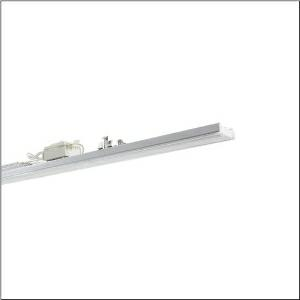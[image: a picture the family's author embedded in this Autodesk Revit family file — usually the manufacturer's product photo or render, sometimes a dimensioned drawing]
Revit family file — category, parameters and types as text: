
# Revit family: licross_r__11_recessed_ho_51tl12dv4m2md_61bc
name_source: partatom
category: Lighting Fixtures
units: mm (PartAtom-declared; Revit-internal decimal feet)

## family parameters
Cut with Voids When Loaded = No
Host = Face
Light Source = No
Part Type = Normal
Room Calculation Point = No
Round Connector Dimension = Use Diameter
Shared = No

## types (1)
- --- (1 x LED, 4070 lm, 21.7 W, 4000K)
    Apparent Load = 22 VA
    CIE Flux Codes = 66 91 98 100 100
    Color Rendering = 80
    Color Temperature = 4000K
    Default Elevation = 1800 mm
    Description = Licross® 11 Recessed HO, luminaire insert, of sheet steel, coil coated, white, length: 2.250mm, width: 66mm, height: 67mm, LED rated luminous flux: 27.150lm, light colour: 840, control gear: DALI 2 (for two DALI lines), with plug, 6-pole, with phase selection, mains connection: 220..240V, AC/DC, 0/50..60Hz, rated input power: 151W, without changeover relay, for emergency light function, for central battery installations according to DIN EN 60598-2-22, halogen-free wiring, primary optical cover: cover, of PMMA, light emission: direct distribution, primary light characteristic: symmetric, protection rating (complete): IP40, insulation class (complete): insulation class I (protective earthing), certification: CE, ENEC, VDE, UKCA, protection symbol: D if used in an environment without relevant dust loads with corresponding accessories, impact resistance: IK06, permissible ambient temperature for indoor applications: -40..+35°C, standard: EN 60598-2-22, corresponds to IFS (International Featured Standards) requirements for safety and quality in the food industry, reducing of maximum allowable ambient temperature of 5°C with ceiling mounting, LABS conformity tested according to VDMA 24364:2018-05, packaging unit: 1 piece
    Height = 58 mm
    Lamp = 1 x LED
    Lamp Light Flux = 4070 lm
    Lamp Power = 21.7 W
    Lamp count = 1
    Length = 2250 mm
    Luminous efficacy = 188 lm/W
    Manufacturer = Siteco
    ModVariant = No
    Model = 51TL12DV4M2MD
    Mounting Place = Ceiling
    Mounting Type = Pendant
    Number of Poles = 1
    OnlyDefault = Yes
    Power Factor = 1
    Product Name = Licross® 11 Recessed HO
    Product group = luminaire insert
    ProductGroupID = 902
    Protection Class = Protection class I
    Protection Degree = IP 40
    RLX_Detail_Level = 1
    RLX_Emergency_Light_Flux = 0 lm
    RLX_Emergency_Type = 0
    RLX_Emergency_Type_DB = No
    RlxData = <blob elided: 30049 chars, md5=9e7dcc5a>
    Socket = socket
    Standby Power = 0 W
    System Light Flux = 4070 lm
    System Power = 22 W
    Type Comments = : DC mode (central or group accumulator) initial emergency light level
    Type Image = l_1296930.jpg
    URL = http://relux.com
    VarID = @adj_087344
    Voltage = 0 V
    Weight = 0.00 kg
    Width = 66 mm

## geometry (parser evidence)
native form markers: Blend x4, Sweep x9
no freeform markers — native parametric forms only
